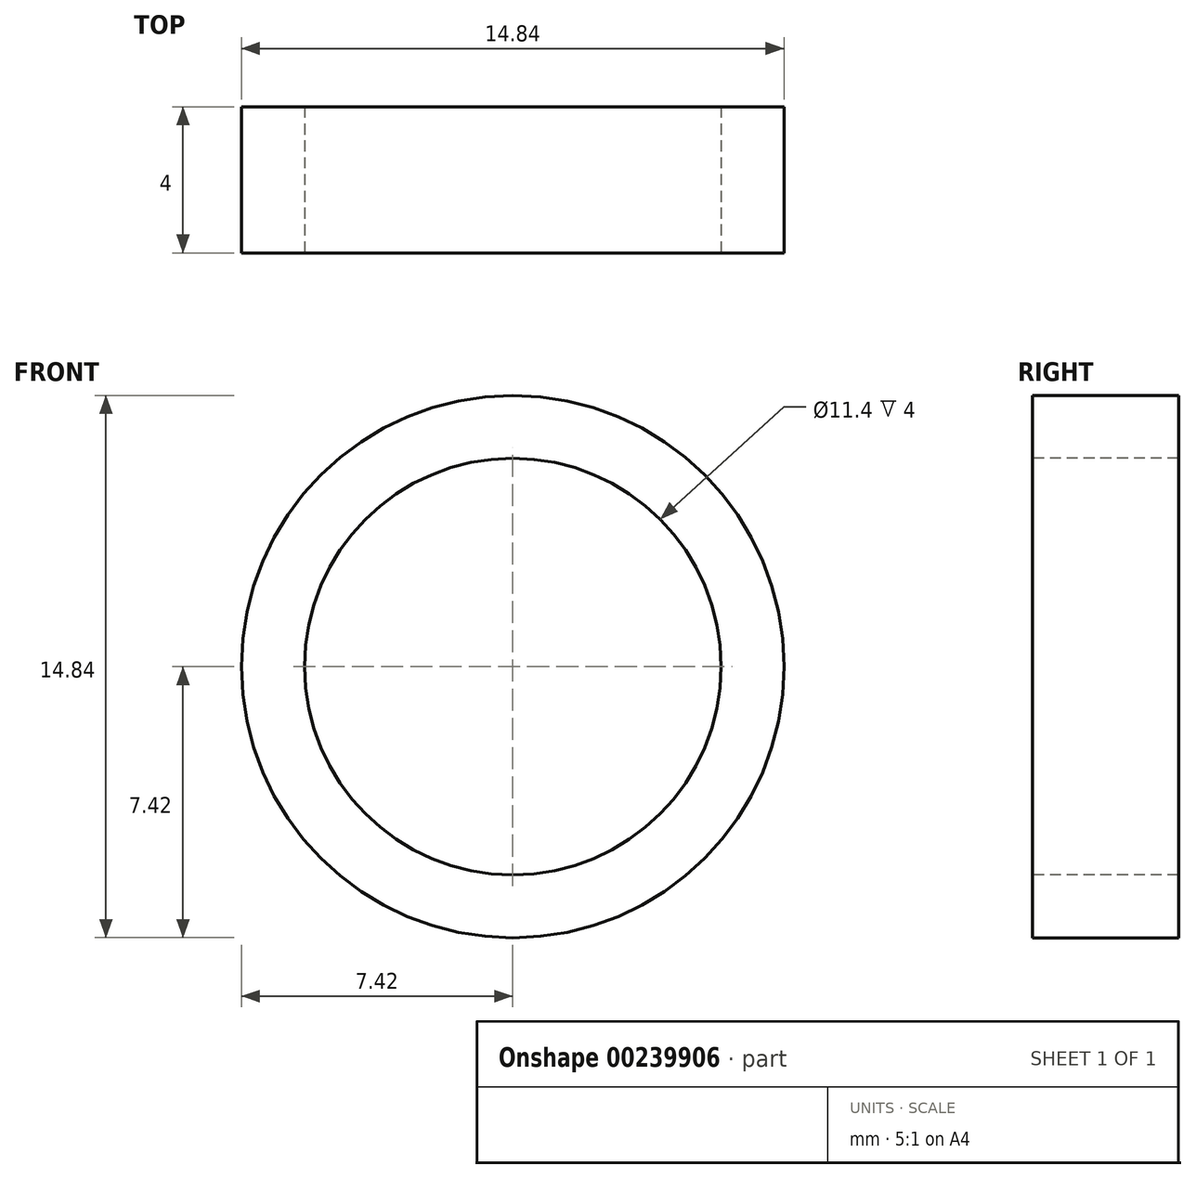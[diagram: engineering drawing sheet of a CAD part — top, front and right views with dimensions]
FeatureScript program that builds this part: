
annotation { "Feature Type Name" : "Feature", "Feature Type Description" : "" }
export const myFeature = defineFeature(function(context is Context, id is Id, definition is map)
    precondition{}
    {
        {
            var Q0;
            Q0=qCreatedBy(makeId("Top.planeOp"),FACE);
            var sketch = newSketch(context, id + "F0", { "sketchPlane" : qUnion([Q0])});
            skLineSegment(sketch, "E0", {"start": v(0, 2.93) * mm, "end": v(0, 2.93) * mm});
            skLineSegment(sketch, "E1", {"start": v(-3, 3.5) * mm, "end": v(0, 3.5) * mm});
            skLineSegment(sketch, "E2", {"start": v(0, 3.5) * mm, "end": v(0, 3.5) * mm});
            skLineSegment(sketch, "E3", {"start": v(-3, 3.5) * mm, "end": v(-3, 6) * mm});
            skLineSegment(sketch, "E4", {"start": v(-3, 6) * mm, "end": v(-5, 6) * mm});
            skLineSegment(sketch, "E5", {"start": v(-5, 2) * mm, "end": v(-5, 6) * mm});
            skLineSegment(sketch, "E6", {"start": v(-5, 2) * mm, "end": v(-13, 2) * mm});
            skLineSegment(sketch, "E7", {"start": v(-13, 6) * mm, "end": v(-13, 2) * mm});
            skLineSegment(sketch, "E8", {"start": v(-3, 6) * mm, "end": v(-13, 6) * mm, "construction": true});
            skLineSegment(sketch, "E9", {"start": v(-13, 6) * mm, "end": v(-16, 6) * mm});
            skLineSegment(sketch, "E10", {"start": v(-16, 6) * mm, "end": v(-16, 0) * mm});
            skLineSegment(sketch, "E11", {"start": v(-16, 0) * mm, "end": v(0, 0) * mm});
            skLineSegment(sketch, "E12", {"start": v(0, 0) * mm, "end": v(0, 3.5) * mm});
            skLineSegment(sketch, "E13", {"start": v(-7.73, -7.75) * mm, "end": v(-7.73, -7.75) * mm});
            skSolve(sketch);
        }
        {
            var Q0;
            Q0=qCreatedBy(makeId("Top.planeOp"),FACE);
            var sketch = newSketch(context, id + "F1", { "sketchPlane" : qUnion([Q0])});
            skLineSegment(sketch, "E14.bottom", {"start": v(-7.42, 6.7) * mm, "end": v(-5.7, 6.7) * mm});
            skLineSegment(sketch, "E14.top", {"start": v(-7.42, 2.7) * mm, "end": v(-5.7, 2.7) * mm});
            skLineSegment(sketch, "E14.left", {"start": v(-7.42, 6.7) * mm, "end": v(-7.42, 2.7) * mm});
            skLineSegment(sketch, "E14.right", {"start": v(-5.7, 6.7) * mm, "end": v(-5.7, 2.7) * mm});
            skSolve(sketch);
        }
        {
            var Q0;
            Q0=makeQuery(id+"F1.imprint","IMPRINT",FACE,{"disambiguationData":[TD([[makeQuery(id+"F1.imprint","IMPRINT",EDGE,{"derivedFrom":sQuery(id+"F1.wireOp",EDGE,"E14.bottom")}),-1.0]])]});
            var Q1;
            Q1=sQuery(id+"F0.wireOp",EDGE,"E12");
            revolve(context, id + "F2", {"entities" : qUnion([Q0]), "axis" : qUnion([Q1]), "revolveType" : RevolveType.FULL});
        }
    });
